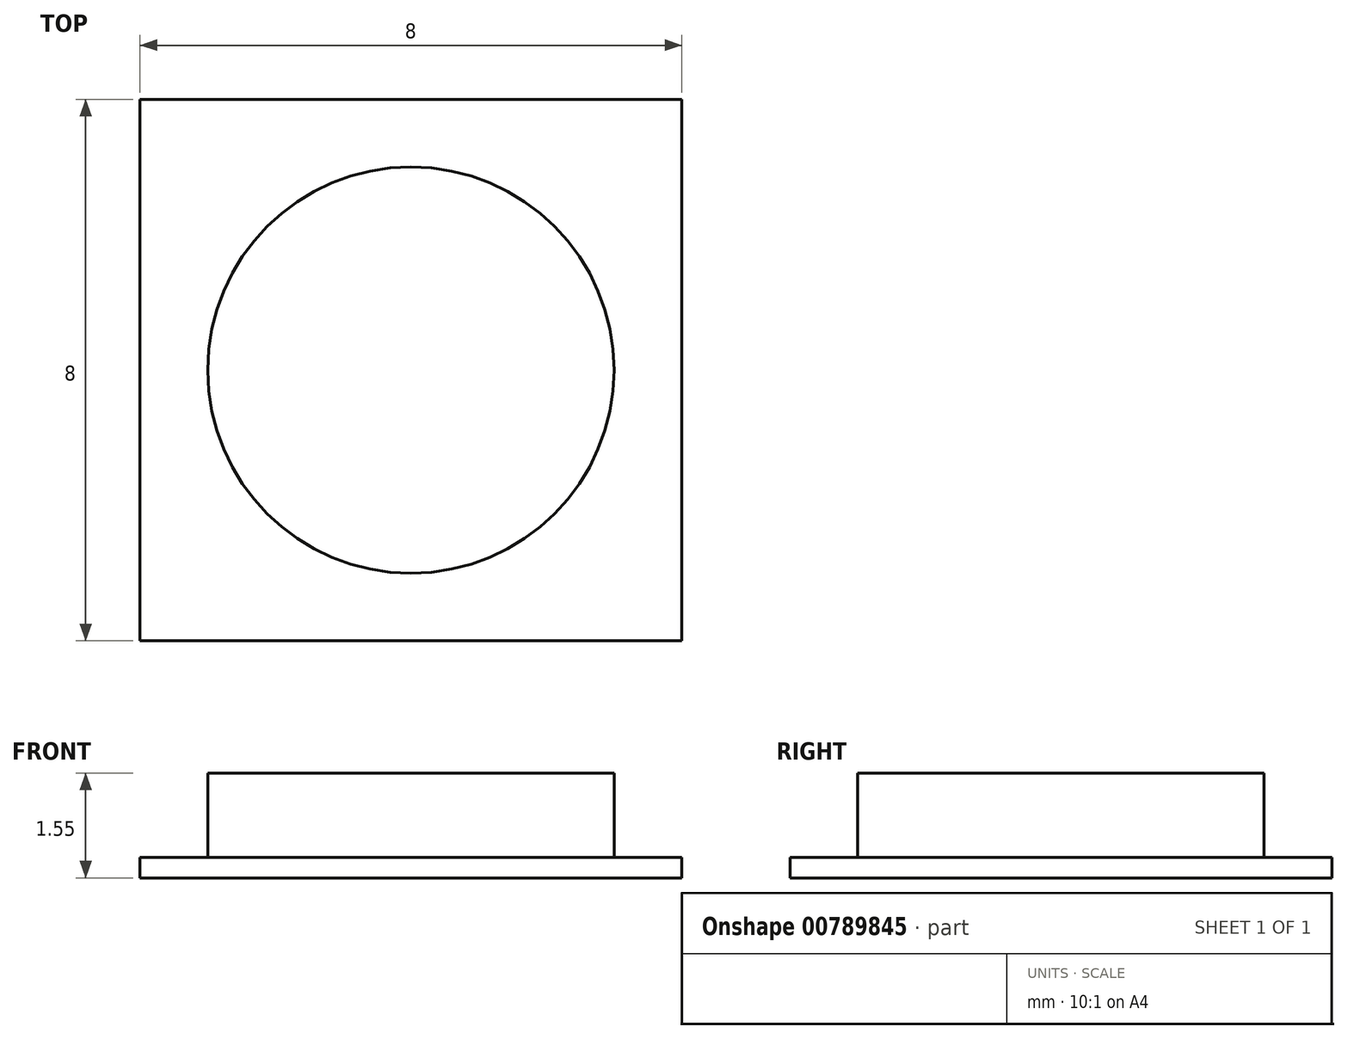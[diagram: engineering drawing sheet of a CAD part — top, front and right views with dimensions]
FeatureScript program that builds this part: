
annotation { "Feature Type Name" : "Feature", "Feature Type Description" : "" }
export const myFeature = defineFeature(function(context is Context, id is Id, definition is map)
    precondition{}
    {
        {
            var Q0;
            Q0=qCreatedBy(makeId("Top.planeOp"),FACE);
            var sketch = newSketch(context, id + "F0", { "sketchPlane" : qUnion([Q0])});
            skLineSegment(sketch, "E0.bottom", {"start": v(4, -4) * mm, "end": v(-4, -4) * mm});
            skLineSegment(sketch, "E0.top", {"start": v(4, 4) * mm, "end": v(-4, 4) * mm});
            skLineSegment(sketch, "E0.left", {"start": v(4, -4) * mm, "end": v(4, 4) * mm});
            skLineSegment(sketch, "E0.right", {"start": v(-4, -4) * mm, "end": v(-4, 4) * mm});
            skPoint(sketch, "E0.middle", {"position": v(0, 0) * mm});
            skSolve(sketch);
        }
        {
            var Q0;
            Q0=qSketchRegion(id+"F0",true);
            extrude(context, id + "F1", {"entities" : qUnion([Q0]), "depth" : 0.3 * mm, "offsetDistance" : 25 * mm});
        }
        {
            var Q0;
            Q0=makeQuery(id+"F1.opExtrude","CAP_FACE",FACE,{"disambiguationData":[OSD([sQuery(id+"F0.wireOp",EDGE,"E0.bottom"),sQuery(id+"F0.wireOp",EDGE,"E0.top"),sQuery(id+"F0.wireOp",EDGE,"E0.left"),sQuery(id+"F0.wireOp",EDGE,"E0.right"),sQuery(id+"F0.wireOp",EDGE,"zQb6MZgK-B0pt-c5tb-Pr6v-ySiWqahg72p7")])],"isStart":false});
            var sketch = newSketch(context, id + "F2", { "sketchPlane" : qUnion([Q0])});
            skCircle(sketch, "E1", {"center": v(0, 0) * mm, "radius": 3 * mm});
            skSolve(sketch);
        }
        {
            var Q0;
            Q0=qSketchRegion(id+"F2",true);
            extrude(context, id + "F3", {"entities" : qUnion([Q0]), "operationType" : NewBodyOperationType.ADD, "depth" : 1.25 * mm, "offsetDistance" : 25 * mm});
        }
    });
